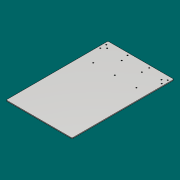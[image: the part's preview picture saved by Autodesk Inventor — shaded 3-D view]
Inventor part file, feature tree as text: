
AUTODESK INVENTOR PART (.ipt)
format: ipt  version: 2018 (Build 220112000, 112)  size: 194,048 bytes
history: native  units: mm
features: extrude x4, sketch x4, projected_geometry x2, other x1, fillet x1
ambient origin geometry x8: Origin, YZ Plane, XZ Plane, XY Plane, X Axis, Y Axis, Z Axis, Center Point
bodies: Body1 (feature_tree)
feature tree (12):
  other  "ソリッド1"
  extrude  "押し出し1"  Depth=23.55mm
  extrude  "押し出し3"  Depth=84.0mm
  extrude  "押し出し4"  Depth=79.0mm
  extrude  "押し出し5"  Depth=78.0mm
  fillet  "フィレット4"  Radius=3.2mm
  sketch  "スケッチ1"
  sketch  "スケッチ3"
  sketch  "スケッチ5"
  projected_geometry  "投影ループ1"
  sketch  "スケッチ6"
  projected_geometry  "投影ループ2"
